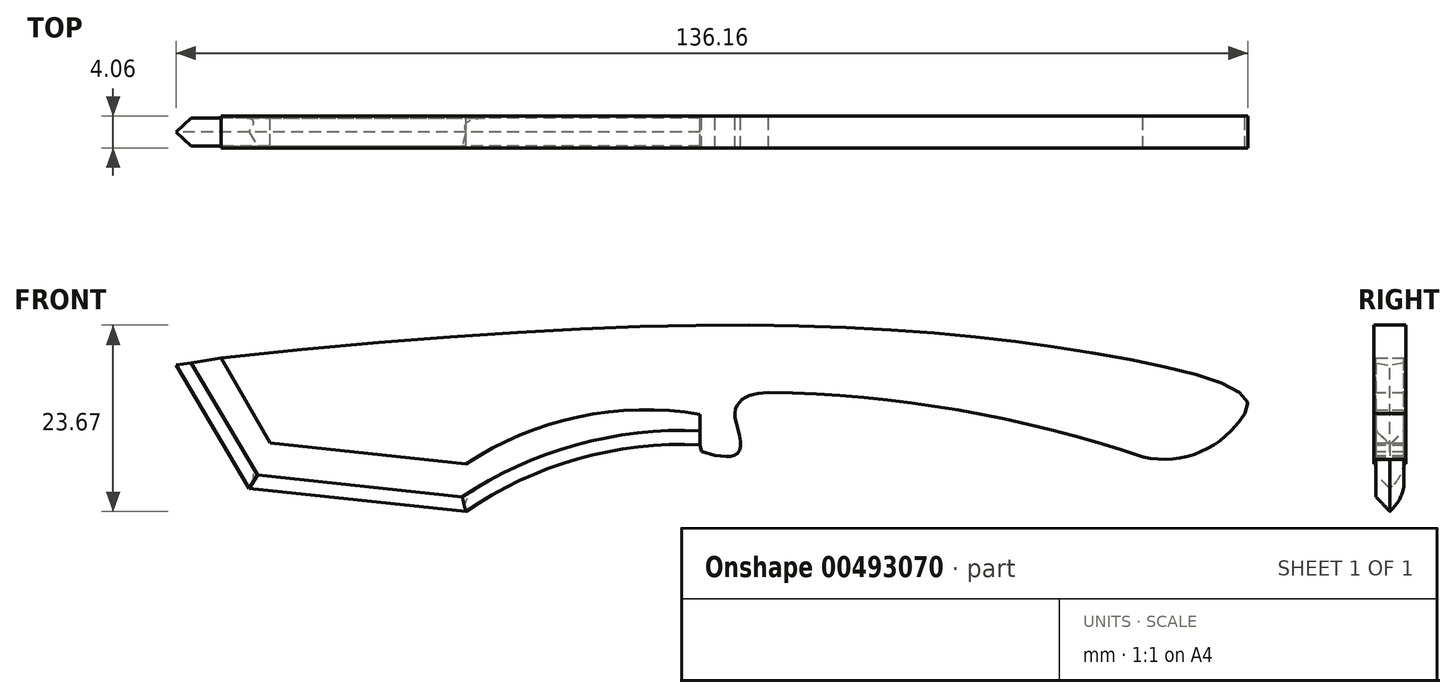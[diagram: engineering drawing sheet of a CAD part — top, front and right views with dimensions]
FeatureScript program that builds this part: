
annotation { "Feature Type Name" : "Feature", "Feature Type Description" : "" }
export const myFeature = defineFeature(function(context is Context, id is Id, definition is map)
    precondition{}
    {
        {
            var Q0;
            Q0=qCreatedBy(makeId("Front.planeOp"),FACE);
            var sketch = newSketch(context, id + "F0", { "sketchPlane" : qUnion([Q0])});
            skFitSpline(sketch, "E0", {"points": [v(-62.75, 28.2) * mm, v(48.53, 28.71) * mm, v(67.28, 21.14) * mm], "startDerivative": vector(244.6, 25.97) * mm, "endDerivative": vector(-26.81, -33.24) * mm});
            skArc(sketch, "E1", {"start": v(54.36, 15.6) * mm, "mid": v(61.71, 16.29) * mm, "end": v(67.28, 21.14) * mm});
            skLineSegment(sketch, "E2", {"start": v(-59.19, 11.64) * mm, "end": v(-31.66, 8.69) * mm});
            skArc(sketch, "E3", {"start": v(54.36, 15.6) * mm, "mid": v(30.9, 21.56) * mm, "end": v(6.79, 23.8) * mm});
            skFitSpline(sketch, "E4", {"points": [v(0, 15.82) * mm, v(2.44, 15.82) * mm, v(3.23, 17.07) * mm, v(2.54, 20.62) * mm, v(2.93, 22.4) * mm, v(4.32, 23.38) * mm, v(6.79, 23.8) * mm], "startDerivative": vector(18.07, -2.86) * mm, "endDerivative": vector(16.44, 1.58) * mm});
            skLineSegment(sketch, "E5", {"start": v(0, 15.82) * mm, "end": v(-1.76, 16.3) * mm});
            skLineSegment(sketch, "E6", {"start": v(-1.76, 16.3) * mm, "end": v(-1.9, 17.16) * mm});
            skArc(sketch, "E7", {"start": v(-1.9, 17.16) * mm, "mid": v(-17.47, 15.35) * mm, "end": v(-31.66, 8.69) * mm});
            skLineSegment(sketch, "E8", {"start": v(-56.56, 17.4) * mm, "end": v(-31.66, 14.72) * mm});
            skLineSegment(sketch, "E9", {"start": v(-1.9, 17.16) * mm, "end": v(-1.9, 21.04) * mm});
            skArc(sketch, "E10", {"start": v(-1.9, 21.04) * mm, "mid": v(-17.38, 20.7) * mm, "end": v(-31.66, 14.72) * mm});
            skLineSegment(sketch, "E11", {"start": v(-56.56, 17.4) * mm, "end": v(-62.75, 28.2) * mm});
            skLineSegment(sketch, "E12", {"start": v(-59.19, 11.64) * mm, "end": v(-68.46, 27.28) * mm});
            skLineSegment(sketch, "E13", {"start": v(-68.46, 27.28) * mm, "end": v(-62.75, 28.2) * mm});
            skLineSegment(sketch, "E14", {"start": v(-56.56, 17.4) * mm, "end": v(-59.19, 11.64) * mm});
            skLineSegment(sketch, "E15", {"start": v(-31.66, 14.72) * mm, "end": v(-31.66, 8.69) * mm});
            skSolve(sketch);
        }
        {
            var Q0;
            Q0=makeQuery(id+"F0.imprint","IMPRINT",FACE,{"disambiguationData":[TD([[makeQuery(id+"F0.imprint","IMPRINT",EDGE,{"derivedFrom":sQuery(id+"F0.wireOp",EDGE,"E0")}),-1.0]])]});
            extrude(context, id + "F1", {"entities" : qUnion([Q0]), "endBound" : BoundingType.SYMMETRIC, "depth" : 4.06 * mm});
        }
        {
            var Q0;
            Q0=makeQuery(id+"F0.imprint","IMPRINT",FACE,{"disambiguationData":[TD([[makeQuery(id+"F0.imprint","IMPRINT",EDGE,{"derivedFrom":sQuery(id+"F0.wireOp",EDGE,"E11")}),1.0]])]});
            var Q1;
            Q1=makeQuery(id+"F0.imprint","IMPRINT",FACE,{"disambiguationData":[TD([[makeQuery(id+"F0.imprint","IMPRINT",EDGE,{"derivedFrom":sQuery(id+"F0.wireOp",EDGE,"E2")}),1.0]])]});
            var Q2;
            Q2=makeQuery(id+"F0.imprint","IMPRINT",FACE,{"disambiguationData":[TD([[makeQuery(id+"F0.imprint","IMPRINT",EDGE,{"derivedFrom":sQuery(id+"F0.wireOp",EDGE,"E7")}),-1.0]])]});
            extrude(context, id + "F2", {"entities" : qUnion([Q0, Q1, Q2]), "endBound" : BoundingType.SYMMETRIC, "depth" : 3.56 * mm});
        }
        {
            var Q0;
            Q0=makeQuery(id+"F2.opExtrude","CAP_EDGE",EDGE,{"disambiguationData":[OSD([sQuery(id+"F0.wireOp",EDGE,"E7")])],"isStart":false});
            var Q1;
            Q1=makeQuery(id+"F2.opExtrude","CAP_EDGE",EDGE,{"disambiguationData":[OSD([sQuery(id+"F0.wireOp",EDGE,"E7")])],"isStart":true});
            var Q2;
            Q2=makeQuery(id+"F2.opExtrude","CAP_EDGE",EDGE,{"disambiguationData":[OSD([sQuery(id+"F0.wireOp",EDGE,"E2")])],"isStart":false});
            var Q3;
            Q3=makeQuery(id+"F2.opExtrude","CAP_EDGE",EDGE,{"disambiguationData":[OSD([sQuery(id+"F0.wireOp",EDGE,"E2")])],"isStart":true});
            var Q4;
            Q4=makeQuery(id+"F2.opExtrude","CAP_EDGE",EDGE,{"disambiguationData":[OSD([sQuery(id+"F0.wireOp",EDGE,"E12")])],"isStart":false});
            var Q5;
            Q5=makeQuery(id+"F2.opExtrude","CAP_EDGE",EDGE,{"disambiguationData":[OSD([sQuery(id+"F0.wireOp",EDGE,"E12")])],"isStart":true});
            chamfer(context, id + "F3", {"entities" : qUnion([Q0, Q1, Q2, Q3, Q4, Q5]), "width" : 1.78 * mm, "tangentPropagation" : true});
        }
        {
            var Q0;
            {var subQ0=sQuery(id+"F0.wireOp",EDGE,"E2");Q0=makeQuery(id+"F3.opChamfer","BLEND_EDGE",EDGE,{"blendedFrom":[makeQuery(id+"F2.opExtrude","CAP_EDGE",EDGE,{"disambiguationData":[OSD([subQ0])],"isStart":true}),makeQuery(id+"F2.opExtrude","CAP_FACE",FACE,{"disambiguationData":[OSD([subQ0,sQuery(id+"F0.wireOp",EDGE,"E7"),sQuery(id+"F0.wireOp",EDGE,"E8"),sQuery(id+"F0.wireOp",EDGE,"E9"),sQuery(id+"F0.wireOp",EDGE,"E10"),sQuery(id+"F0.wireOp",EDGE,"E11"),sQuery(id+"F0.wireOp",EDGE,"E12"),sQuery(id+"F0.wireOp",EDGE,"E13")])],"isStart":true})],"blendedInto":[makeQuery(id+"F2.opExtrude","CAP_FACE",FACE,{"disambiguationData":[OSD([subQ0,sQuery(id+"F0.wireOp",EDGE,"E7"),sQuery(id+"F0.wireOp",EDGE,"E8"),sQuery(id+"F0.wireOp",EDGE,"E9"),sQuery(id+"F0.wireOp",EDGE,"E10"),sQuery(id+"F0.wireOp",EDGE,"E11"),sQuery(id+"F0.wireOp",EDGE,"E12"),sQuery(id+"F0.wireOp",EDGE,"E13")])],"isStart":true})]});}
            fillet(context, id + "F4", {"entities" : qUnion([Q0]), "radius" : 5.08 * mm, "tangentPropagation" : true, "allowEdgeOverflow" : false});
        }
    });
